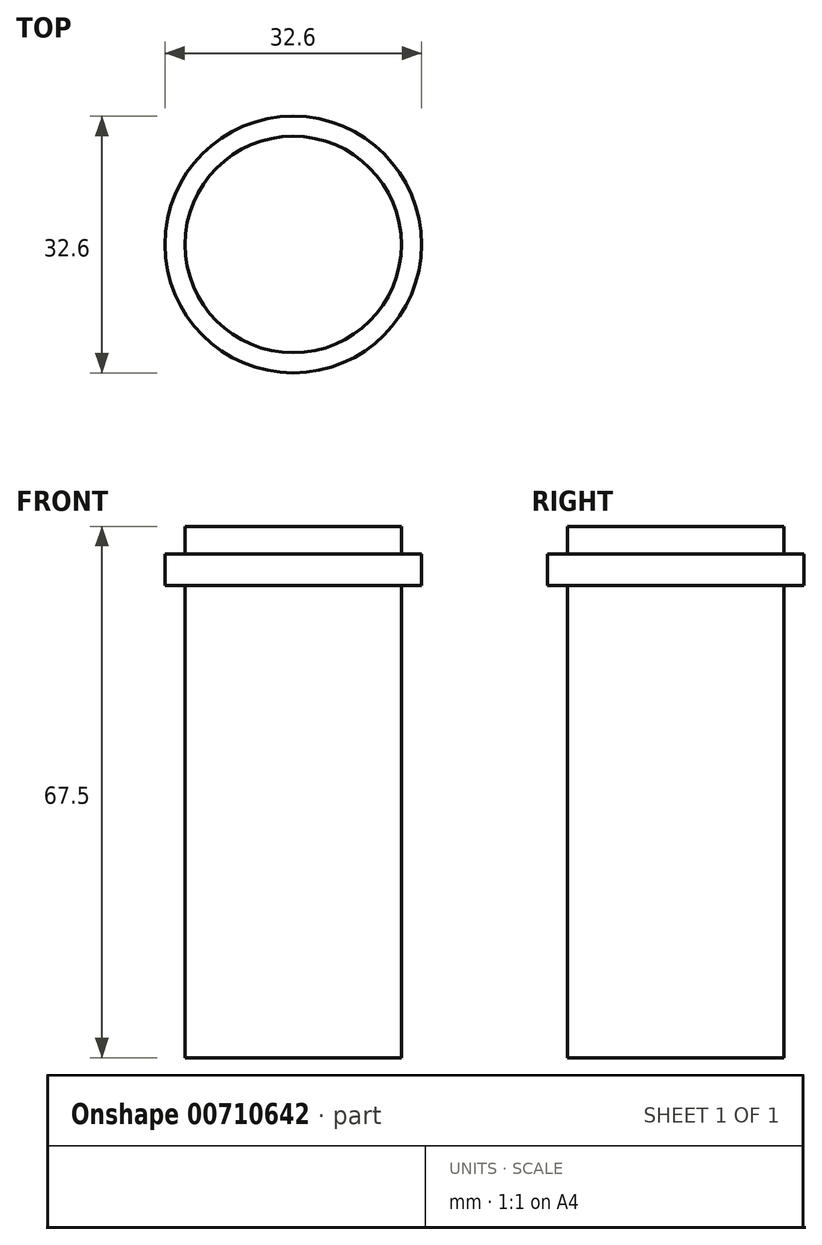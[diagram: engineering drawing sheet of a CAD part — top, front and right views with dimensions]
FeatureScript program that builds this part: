
annotation { "Feature Type Name" : "Feature", "Feature Type Description" : "" }
export const myFeature = defineFeature(function(context is Context, id is Id, definition is map)
    precondition{}
    {
        {
            var Q0;
            Q0=qCreatedBy(makeId("Front.planeOp"),FACE);
            var sketch = newSketch(context, id + "F0", { "sketchPlane" : qUnion([Q0])});
            skLineSegment(sketch, "E0", {"start": v(0, 25.83) * mm, "end": v(-13.75, 25.83) * mm});
            skLineSegment(sketch, "E1", {"start": v(-13.75, 25.83) * mm, "end": v(-13.75, 22.33) * mm});
            skLineSegment(sketch, "E2", {"start": v(-13.75, 22.33) * mm, "end": v(-16.3, 22.33) * mm});
            skLineSegment(sketch, "E3", {"start": v(-16.3, 22.33) * mm, "end": v(-16.3, 18.33) * mm});
            skLineSegment(sketch, "E4", {"start": v(-16.3, 18.33) * mm, "end": v(-13.75, 18.33) * mm});
            skLineSegment(sketch, "E5", {"start": v(-13.75, 18.33) * mm, "end": v(-13.75, -41.67) * mm});
            skLineSegment(sketch, "E6", {"start": v(-13.75, -41.67) * mm, "end": v(0, -41.67) * mm});
            skLineSegment(sketch, "E7", {"start": v(0, 25.83) * mm, "end": v(0, -41.67) * mm});
            skSolve(sketch);
        }
        {
            var Q0;
            Q0 = qSketchRegion(id + "F0", true);
            var Q1;
            Q1=sQuery(id+"F0.wireOp",EDGE,"E7");
            revolve(context, id + "F1", {"surfaceOperationType" : NewSurfaceOperationType.NEW, "entities" : qUnion([Q0]), "axis" : qUnion([Q1]), "revolveType" : RevolveType.FULL});
        }
    });
